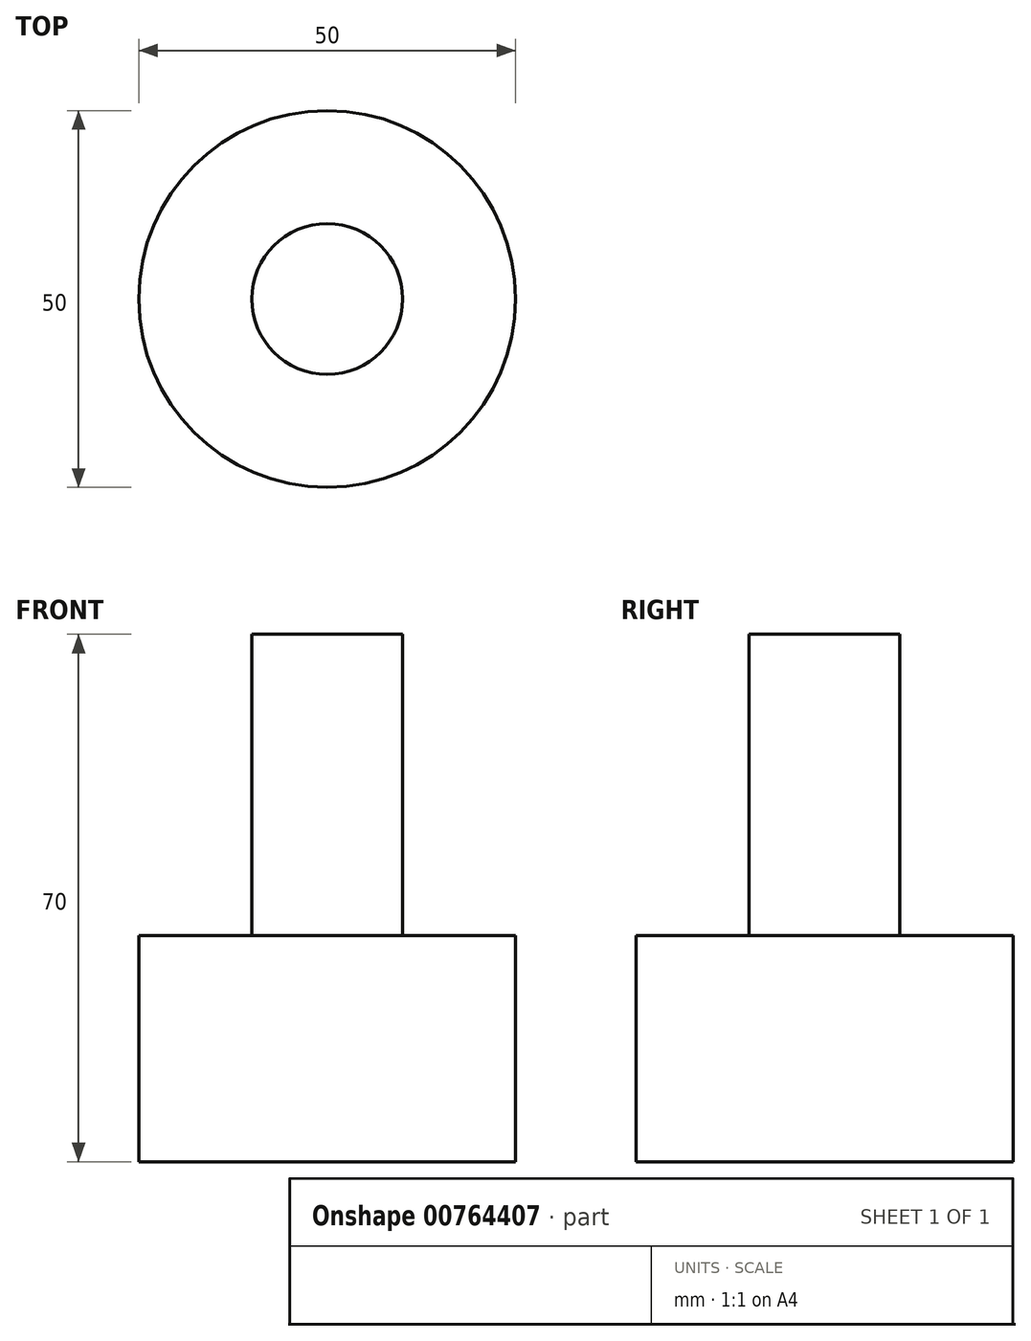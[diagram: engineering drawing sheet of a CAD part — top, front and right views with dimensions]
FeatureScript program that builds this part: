
annotation { "Feature Type Name" : "Feature", "Feature Type Description" : "" }
export const myFeature = defineFeature(function(context is Context, id is Id, definition is map)
    precondition{}
    {
        {
            var Q0;
            Q0=qCreatedBy(makeId("Top.planeOp"),FACE);
            var sketch = newSketch(context, id + "F0", { "sketchPlane" : qUnion([Q0])});
            skCircle(sketch, "E0", {"center": v(0, 0) * mm, "radius": 25 * mm});
            skSolve(sketch);
        }
        {
            var Q0;
            Q0 = qSketchRegion(id + "F0", true);
            extrude(context, id + "F1", {"entities" : qUnion([Q0]), "endBound" : BoundingType.SYMMETRIC, "oppositeDirection" : true, "depth" : 30 * mm, "offsetDistance" : 25.4 * mm});
        }
        {
            var Q0;
            Q0=makeQuery(id+"F1.opExtrude","CAP_FACE",FACE,{"disambiguationData":[OSD([sQuery(id+"F0.wireOp",EDGE,"E0")])],"isStart":true});
            var sketch = newSketch(context, id + "F2", { "sketchPlane" : qUnion([Q0])});
            skCircle(sketch, "E1", {"center": v(0, 0) * mm, "radius": 10 * mm});
            skSolve(sketch);
        }
        {
            var Q0;
            Q0=makeQuery(id+"F2.imprint","IMPRINT",FACE,{"disambiguationData":[TD([[makeQuery(id+"F2.imprint","IMPRINT",EDGE,{"derivedFrom":sQuery(id+"F2.wireOp",EDGE,"E1")}),1.0]])]});
            extrude(context, id + "F3", {"entities" : qUnion([Q0]), "operationType" : NewBodyOperationType.ADD, "depth" : 40 * mm, "offsetDistance" : 25.4 * mm});
        }
    });
